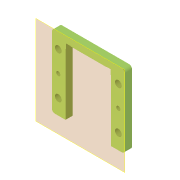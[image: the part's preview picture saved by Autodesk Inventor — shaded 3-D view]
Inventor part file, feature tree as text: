
AUTODESK INVENTOR PART (.ipt)
format: ipt  version: 2022 (Build 260153000, 153)  size: 189,952 bytes
history: native  units: mm
features: other x9, reference x8, sketch x3, hole x2, extrude x1, plane x1
ambient origin geometry x8: Origin, YZ Plane, XZ Plane, XY Plane, X Axis, Y Axis, Z Axis, Center Point
bodies: Solid1 (feature_tree)
feature tree (24):
  extrude  "Extrusion1"  Depth=5.0mm TaperAngle=0.0deg
  plane  "Arbeitsebene1"
  hole  "Bohrung1"  [1 undecoded]
  hole  "Bohrung5"  [1 undecoded]
  sketch  "Sketch1"  dims[d0=7.8mm d1=5.0mm d2=0.0mm]
  reference  "Reference1"
  reference  "Reference2"
  reference  "Reference3"
  sketch  "Skizze3"  dims[d7=4.6mm d8=6.0mm d9=4.0mm d10=2.0mm d11=90.0deg d12=8.0mm d13=20.594885mm d23=1.5mm]
  reference  "Referenz4"
  reference  "Referenz5"
  reference  "Referenz14"
  sketch  "Skizze10"  dims[d24=1.5mm d57=0.2mm d62=2.8mm d63=6.0mm d64=6.0mm d65=3.0mm d66=90.0deg d67=8.0mm d68=20.594885mm]
  reference  "Referenz15"
  reference  "Referenz16"
  other  "Assembly_Cube_Z-Stage_NEMA11_china_Borstel.iam"
  other  "00_Linear_Stage_NEMA11_Mount:1"
  other  "10_Base_puzzle_IM:2"
  other  "Assembly_Cube_Z-Stage_NEMA11_china_multidirection.iam"
  other  "300_Linear_Stage_NEMA11_China_base:1"
  other  "Assembly_Cube_Z-Stage_NEMA11_china_universal_25mm.iam"
  other  "00_Linear_Stage_NEMA11_25mm_china:1"
  other  "Actuator_movable"
  other  "30_Linear_Stage_NEMA11_China_base_universal_v2:1"
note: 2 required parameter values undecoded (feature->parameter linkage not recoverable at this tier; creation-order binding heuristic only, values carry confidence <= 0.55)
